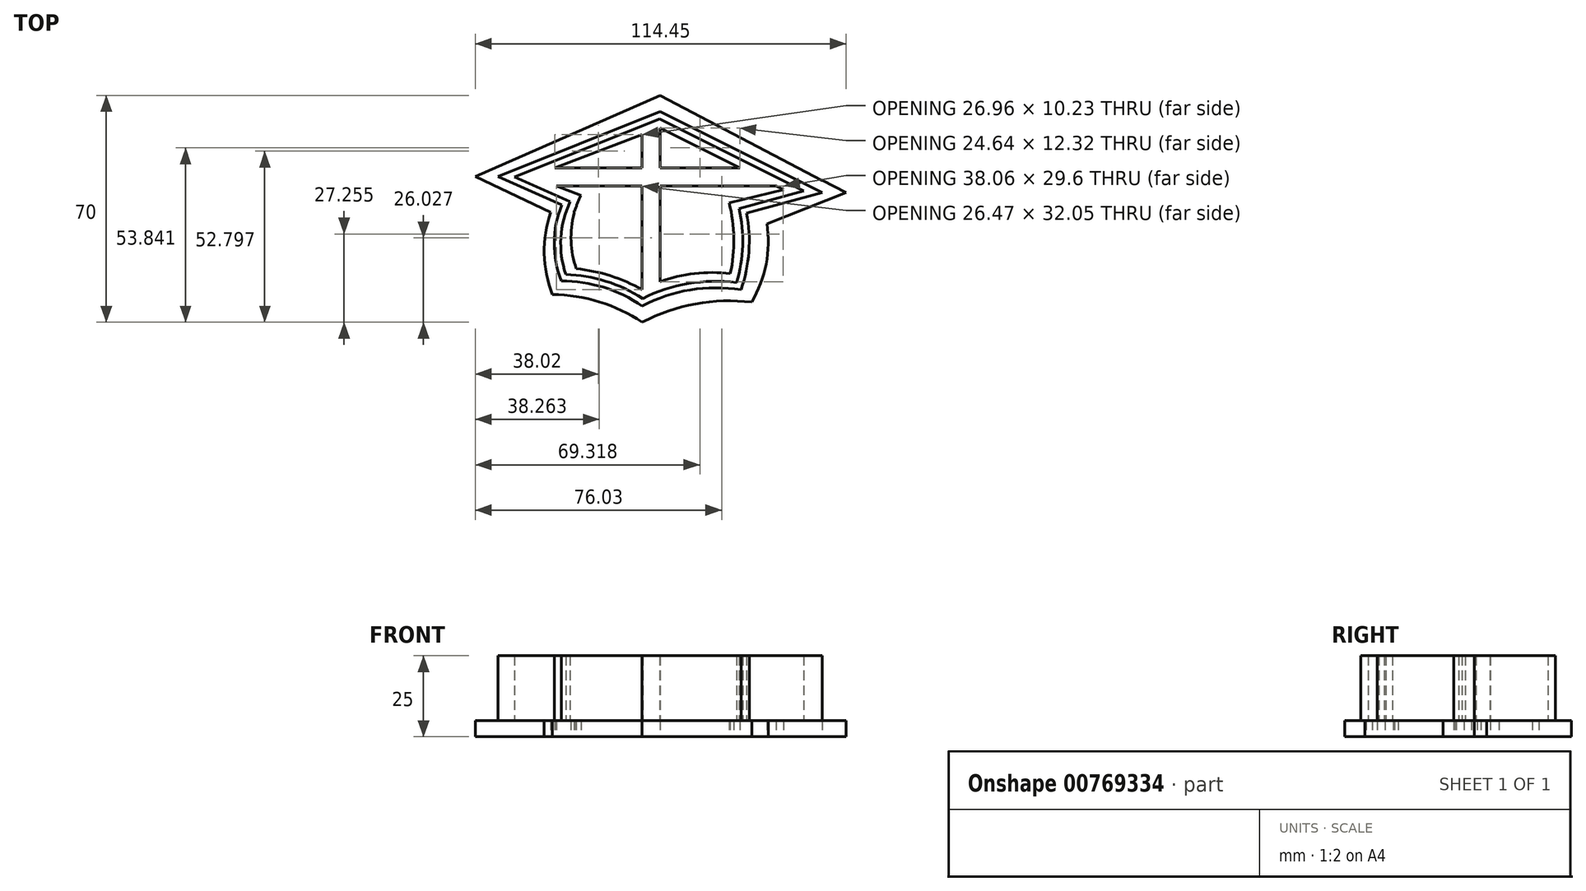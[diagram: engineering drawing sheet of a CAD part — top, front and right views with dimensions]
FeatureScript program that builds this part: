
annotation { "Feature Type Name" : "Feature", "Feature Type Description" : "" }
export const myFeature = defineFeature(function(context is Context, id is Id, definition is map)
    precondition{}
    {
        {
            var Q0;
            Q0=qCreatedBy(makeId("Top.planeOp"),FACE);
            var sketch = newSketch(context, id + "F0", { "sketchPlane" : qUnion([Q0])});
            skLineSegment(sketch, "E0.bottom", {"start": v(50, 50) * mm, "end": v(-50, 50) * mm});
            skLineSegment(sketch, "E0.top", {"start": v(50, -50) * mm, "end": v(-50, -50) * mm});
            skLineSegment(sketch, "E0.left", {"start": v(50, 50) * mm, "end": v(50, -50) * mm});
            skLineSegment(sketch, "E0.right", {"start": v(-50, 50) * mm, "end": v(-50, -50) * mm});
            skPoint(sketch, "E0.middle", {"position": v(0, 0) * mm});
            skLineSegment(sketch, "E1", {"start": v(0, 32.68) * mm, "end": v(0, 30) * mm});
            skLineSegment(sketch, "E2", {"start": v(0, 45) * mm, "end": v(0, 25) * mm});
            skLineSegment(sketch, "E3", {"start": v(35, 25) * mm, "end": v(34.13, 25) * mm});
            skLineSegment(sketch, "E4", {"start": v(0, -10) * mm, "end": v(-5.5, -10) * mm});
            skLineSegment(sketch, "E5", {"start": v(-5.5, -10) * mm, "end": v(-5.5, -5) * mm});
            skArc(sketch, "E6", {"start": v(25, -5) * mm, "mid": v(9.34, -5.03) * mm, "end": v(-5.5, -10) * mm});
            skArc(sketch, "E7", {"start": v(25, -5) * mm, "mid": v(27.54, 10) * mm, "end": v(25, 25) * mm});
            skLineSegment(sketch, "E8", {"start": v(0, 45) * mm, "end": v(0, 10) * mm});
            skLineSegment(sketch, "E9", {"start": v(-50, 30) * mm, "end": v(0, 50) * mm});
            skLineSegment(sketch, "E10", {"start": v(50, 25) * mm, "end": v(0, 50) * mm});
            skLineSegment(sketch, "E11", {"start": v(0, 45) * mm, "end": v(0, 32.68) * mm});
            skLineSegment(sketch, "E12", {"start": v(-50, 30) * mm, "end": v(-30.35, 21.17) * mm});
            skLineSegment(sketch, "E13", {"start": v(50, 25) * mm, "end": v(22.23, 17.5) * mm});
            skLineSegment(sketch, "E14", {"start": v(-5.5, -10) * mm, "end": v(-5.5, -2.25) * mm});
            skPoint(sketch, "E14.endSnap0", {"position": v(-5.5, -7.5) * mm});
            skLineSegment(sketch, "E15", {"start": v(-5.5, -2.25) * mm, "end": v(-30.5, -2.25) * mm});
            skLineSegment(sketch, "E16", {"start": v(-30.5, -2.25) * mm, "end": v(-26.5, -2.25) * mm});
            skLineSegment(sketch, "E17", {"start": v(-26.5, -2.25) * mm, "end": v(-26.5, 3.69) * mm});
            skArc(sketch, "E18", {"start": v(-5.5, -10) * mm, "mid": v(-17.41, -4.23) * mm, "end": v(-30.5, -2.25) * mm});
            skArc(sketch, "E19", {"start": v(-30.35, 21.17) * mm, "mid": v(-32.65, 9.47) * mm, "end": v(-30.5, -2.25) * mm});
            skLineSegment(sketch, "E20", {"start": v(35, 20.95) * mm, "end": v(35.5, 20.95) * mm});
            skLineSegment(sketch, "E21", {"start": v(0, 55) * mm, "end": v(57, 25) * mm});
            skLineSegment(sketch, "E22", {"start": v(-57, 30) * mm, "end": v(0, 55) * mm});
            skLineSegment(sketch, "E23", {"start": v(-57, 30) * mm, "end": v(-33.7, 18.9) * mm});
            skArc(sketch, "E24", {"start": v(-33.7, 18.9) * mm, "mid": v(-35.75, 6.17) * mm, "end": v(-33.19, -6.47) * mm});
            skLineSegment(sketch, "E25", {"start": v(-5.5, -10) * mm, "end": v(-5.5, -15) * mm});
            skArc(sketch, "E26", {"start": v(-5.5, -15) * mm, "mid": v(-18.72, -8.73) * mm, "end": v(-33.19, -6.47) * mm});
            skLineSegment(sketch, "E27", {"start": v(33.01, 15.41) * mm, "end": v(57.45, 25) * mm});
            skArc(sketch, "E28", {"start": v(28.28, -8.77) * mm, "mid": v(32.74, 2.91) * mm, "end": v(33.01, 15.41) * mm});
            skArc(sketch, "E29", {"start": v(28.28, -8.77) * mm, "mid": v(10.93, -9.38) * mm, "end": v(-5.5, -15) * mm});
            skLineSegment(sketch, "E30", {"start": v(0, 45) * mm, "end": v(-39.53, 30) * mm});
            skLineSegment(sketch, "E31", {"start": v(-39.53, 30) * mm, "end": v(-24.42, 24.1) * mm});
            skLineSegment(sketch, "E32", {"start": v(0, 45) * mm, "end": v(38.06, 25.97) * mm});
            skLineSegment(sketch, "E33", {"start": v(38.06, 25.97) * mm, "end": v(21.32, 21.84) * mm});
            skArc(sketch, "E34", {"start": v(-24.42, 24.1) * mm, "mid": v(-27.43, 12.95) * mm, "end": v(-25.83, 1.51) * mm});
            skArc(sketch, "E35", {"start": v(-5.5, -5) * mm, "mid": v(-15.32, -0.68) * mm, "end": v(-25.83, 1.51) * mm});
            skArc(sketch, "E36", {"start": v(21.68, 0) * mm, "mid": v(7.7, -0.42) * mm, "end": v(-5.5, -5) * mm});
            skArc(sketch, "E37", {"start": v(21.68, 0) * mm, "mid": v(22.8, 10.94) * mm, "end": v(21.32, 21.84) * mm});
            skLineSegment(sketch, "E38", {"start": v(-5.5, -5) * mm, "end": v(-5.5, 27.05) * mm});
            skPoint(sketch, "E39.endSnap0", {"position": v(2, -5) * mm});
            skLineSegment(sketch, "E40", {"start": v(-31.97, 27.05) * mm, "end": v(-5.5, 27.05) * mm});
            skLineSegment(sketch, "E41", {"start": v(35.9, 27.05) * mm, "end": v(24.64, 32.68) * mm});
            skLineSegment(sketch, "E42", {"start": v(24.64, 32.68) * mm, "end": v(0, 32.68) * mm});
            skLineSegment(sketch, "E43.trimOffspring", {"start": v(34.13, 25) * mm, "end": v(35, 25) * mm});
            skPoint(sketch, "E44.orphan", {"position": v(-37.04, 16.62) * mm});
            skPoint(sketch, "E45.orphan", {"position": v(2, 44) * mm});
            skPoint(sketch, "E46.trimOffspring.end.orphan", {"position": v(9.5, -5) * mm});
            skPoint(sketch, "E47.orphan", {"position": v(-30.35, 15) * mm});
            skLineSegment(sketch, "E48.trimOffspring", {"start": v(-26.5, 18.63) * mm, "end": v(-26.5, 19.44) * mm});
            skLineSegment(sketch, "E49.trimOffspring", {"start": v(-26.5, 19.44) * mm, "end": v(-26.3, 19.35) * mm});
            skLineSegment(sketch, "E50.trimOffspring", {"start": v(-5.5, 32.68) * mm, "end": v(-5.5, 42.91) * mm});
            skLineSegment(sketch, "E51.trimOffspring", {"start": v(-5.5, 32.68) * mm, "end": v(-32.46, 32.68) * mm});
            skLineSegment(sketch, "E52.trimOffspring", {"start": v(0, 27.05) * mm, "end": v(35.9, 27.05) * mm});
            skLineSegment(sketch, "E53.trimOffspring", {"start": v(0, 30) * mm, "end": v(0, 15) * mm});
            skLineSegment(sketch, "E54.trimOffspring", {"start": v(0, 30) * mm, "end": v(0, 10) * mm});
            skLineSegment(sketch, "E55", {"start": v(0, 10) * mm, "end": v(0, -2.54) * mm});
            skLineSegment(sketch, "E56", {"start": v(26.7, 18.7) * mm, "end": v(50, 25) * mm});
            skLineSegment(sketch, "E57", {"start": v(0, 55) * mm, "end": v(57.45, 25) * mm});
            skSolve(sketch);
        }
        {
            var Q0;
            Q0=makeQuery(id+"F0.imprint","IMPRINT",FACE,{"disambiguationData":[TD([[makeQuery(id+"F0.imprint","IMPRINT",EDGE,{"derivedFrom":sQuery(id+"F0.wireOp",EDGE,"E9")}),-1.0]])]});
            var Q1;
            {var subQ3=sQuery(id+"F0.wireOp",EDGE,"E17");Q1=makeQuery(id+"F0.imprint","IMPRINT",FACE,{"disambiguationData":[TD([[makeQuery(id+"F0.imprint","IMPRINT",EDGE,{"derivedFrom":subQ3}),-1.0]])]});}
            var Q2;
            {var subQ6=sQuery(id+"F0.wireOp",EDGE,"E5");Q2=makeQuery(id+"F0.imprint","IMPRINT",FACE,{"disambiguationData":[TD([[makeQuery(id+"F0.imprint","IMPRINT",EDGE,{"derivedFrom":subQ6}),-1.0]])]});}
            var Q3;
            {var subQ5=sQuery(id+"F0.wireOp",EDGE,"E5");Q3=makeQuery(id+"F0.imprint","IMPRINT",FACE,{"disambiguationData":[TD([[makeQuery(id+"F0.imprint","IMPRINT",EDGE,{"derivedFrom":subQ5}),1.0]])]});}
            var Q4;
            {var subQ0=sQuery(id+"F0.wireOp",EDGE,"E14");Q4=makeQuery(id+"F0.imprint","IMPRINT",FACE,{"disambiguationData":[TD([[makeQuery(id+"F0.imprint","IMPRINT",EDGE,{"derivedFrom":subQ0}),1.0]])]});}
            var Q5;
            {var subQ14=sQuery(id+"F0.wireOp",EDGE,"E1");Q5=makeQuery(id+"F0.imprint","IMPRINT",FACE,{"disambiguationData":[TD([[makeQuery(id+"F0.imprint","IMPRINT",EDGE,{"derivedFrom":subQ14}),-1.0]])]});}
            var Q6;
            {var subQ15=sQuery(id+"F0.wireOp",EDGE,"E52.trimOffspring");Q6=makeQuery(id+"F0.imprint","IMPRINT",FACE,{"disambiguationData":[TD([[makeQuery(id+"F0.imprint","IMPRINT",EDGE,{"derivedFrom":subQ15}),-1.0]])]});}
            var Q7;
            {var subQ0=sQuery(id+"F0.wireOp",EDGE,"E13");var subQ1=sQuery(id+"F0.wireOp",EDGE,"E7");var subQ2=makeQuery(id+"F0.imprint","INTERSECT",VERTEX,{"derivedFrom":[subQ1,subQ0]});Q7=makeQuery(id+"F0.imprint","IMPRINT",FACE,{"disambiguationData":[TD([[makeQuery(id+"F0.imprint","IMPRINT",EDGE,{"disambiguationData":[TD([[subQ2,-1.0]])],"derivedFrom":subQ1}),1.0]])]});}
            var Q8;
            {var subQ4=sQuery(id+"F0.wireOp",EDGE,"E1");Q8=makeQuery(id+"F0.imprint","IMPRINT",FACE,{"disambiguationData":[TD([[makeQuery(id+"F0.imprint","IMPRINT",EDGE,{"derivedFrom":subQ4}),1.0]])]});}
            var Q9;
            {var subQ0=sQuery(id+"F0.wireOp",EDGE,"E42");Q9=makeQuery(id+"F0.imprint","IMPRINT",FACE,{"disambiguationData":[TD([[makeQuery(id+"F0.imprint","IMPRINT",EDGE,{"derivedFrom":subQ0}),-1.0]])]});}
            var Q10;
            {var subQ0=sQuery(id+"F0.wireOp",EDGE,"E50.trimOffspring");Q10=makeQuery(id+"F0.imprint","IMPRINT",FACE,{"disambiguationData":[TD([[makeQuery(id+"F0.imprint","IMPRINT",EDGE,{"derivedFrom":subQ0}),1.0]])]});}
            var Q11;
            {var subQ6=sQuery(id+"F0.wireOp",EDGE,"E38");Q11=makeQuery(id+"F0.imprint","IMPRINT",FACE,{"disambiguationData":[TD([[makeQuery(id+"F0.imprint","IMPRINT",EDGE,{"derivedFrom":subQ6}),1.0]])]});}
            var Q12;
            {var subQ0=sQuery(id+"F0.wireOp",EDGE,"E48.trimOffspring");Q12=makeQuery(id+"F0.imprint","IMPRINT",FACE,{"disambiguationData":[TD([[makeQuery(id+"F0.imprint","IMPRINT",EDGE,{"derivedFrom":subQ0}),-1.0]])]});}
            extrude(context, id + "F1", {"entities" : qUnion([Q0, Q1, Q2, Q3, Q4, Q5, Q6, Q7, Q8, Q9, Q10, Q11, Q12]), "depth" : 25 * mm, "offsetDistance" : 25 * mm});
        }
        {
            var Q0;
            Q0=makeQuery(id+"F1.opExtrude","CAP_FACE",FACE,{"disambiguationData":[OSD([sQuery(id+"F0.wireOp",EDGE,"E6"),sQuery(id+"F0.wireOp",EDGE,"E7"),sQuery(id+"F0.wireOp",EDGE,"E9"),sQuery(id+"F0.wireOp",EDGE,"E10"),sQuery(id+"F0.wireOp",EDGE,"E12"),sQuery(id+"F0.wireOp",EDGE,"E13"),sQuery(id+"F0.wireOp",EDGE,"E18"),sQuery(id+"F0.wireOp",EDGE,"E19")])],"isStart":false});
            shell(context, id + "F2", {"entities" : qUnion([Q0]), "thickness" : 2 * mm});
        }
        {
            var Q0;
            {var subQ6=sQuery(id+"F0.wireOp",EDGE,"E6");Q0=makeQuery(id+"F0.imprint","IMPRINT",FACE,{"disambiguationData":[TD([[makeQuery(id+"F0.imprint","IMPRINT",EDGE,{"derivedFrom":subQ6}),1.0]])]});}
            var Q1;
            {var subQ3=sQuery(id+"F0.wireOp",EDGE,"E10");Q1=makeQuery(id+"F0.imprint","IMPRINT",FACE,{"disambiguationData":[TD([[makeQuery(id+"F0.imprint","IMPRINT",EDGE,{"derivedFrom":subQ3}),-1.0]])]});}
            var Q2;
            {var subQ0=sQuery(id+"F0.wireOp",EDGE,"E0.bottom");var subQ2=sQuery(id+"F0.wireOp",EDGE,"E22");var subQ3=makeQuery(id+"F0.imprint","INTERSECT",VERTEX,{"derivedFrom":[subQ0,subQ2]});Q2=makeQuery(id+"F0.imprint","IMPRINT",FACE,{"disambiguationData":[TD([[makeQuery(id+"F0.imprint","IMPRINT",EDGE,{"disambiguationData":[TD([[subQ3,1.0]])],"derivedFrom":subQ0}),-1.0]])]});}
            var Q3;
            {var subQ0=sQuery(id+"F0.wireOp",EDGE,"E9");Q3=makeQuery(id+"F0.imprint","IMPRINT",FACE,{"disambiguationData":[TD([[makeQuery(id+"F0.imprint","IMPRINT",EDGE,{"derivedFrom":subQ0}),1.0]])]});}
            var Q4;
            {var subQ1=sQuery(id+"F0.wireOp",EDGE,"E0.right");var subQ4=sQuery(id+"F0.wireOp",EDGE,"E22");var subQ5=makeQuery(id+"F0.imprint","INTERSECT",VERTEX,{"derivedFrom":[subQ1,subQ4]});Q4=makeQuery(id+"F0.imprint","IMPRINT",FACE,{"disambiguationData":[TD([[makeQuery(id+"F0.imprint","IMPRINT",EDGE,{"disambiguationData":[TD([[subQ5,1.0]])],"derivedFrom":subQ4}),-1.0]])]});}
            var Q5;
            {var subQ0=sQuery(id+"F0.wireOp",EDGE,"E12");Q5=makeQuery(id+"F0.imprint","IMPRINT",FACE,{"disambiguationData":[TD([[makeQuery(id+"F0.imprint","IMPRINT",EDGE,{"derivedFrom":subQ0}),-1.0]])]});}
            var Q6;
            {var subQ6=sQuery(id+"F0.wireOp",EDGE,"E5");Q6=makeQuery(id+"F0.imprint","IMPRINT",FACE,{"disambiguationData":[TD([[makeQuery(id+"F0.imprint","IMPRINT",EDGE,{"derivedFrom":subQ6}),-1.0]])]});}
            var Q7;
            {var subQ5=sQuery(id+"F0.wireOp",EDGE,"E5");Q7=makeQuery(id+"F0.imprint","IMPRINT",FACE,{"disambiguationData":[TD([[makeQuery(id+"F0.imprint","IMPRINT",EDGE,{"derivedFrom":subQ5}),1.0]])]});}
            var Q8;
            {var subQ3=sQuery(id+"F0.wireOp",EDGE,"E17");Q8=makeQuery(id+"F0.imprint","IMPRINT",FACE,{"disambiguationData":[TD([[makeQuery(id+"F0.imprint","IMPRINT",EDGE,{"derivedFrom":subQ3}),-1.0]])]});}
            var Q9;
            Q9=makeQuery(id+"F0.imprint","IMPRINT",FACE,{"disambiguationData":[TD([[makeQuery(id+"F0.imprint","IMPRINT",EDGE,{"derivedFrom":sQuery(id+"F0.wireOp",EDGE,"E9")}),-1.0]])]});
            var Q10;
            {var subQ0=sQuery(id+"F0.wireOp",EDGE,"E13");var subQ1=sQuery(id+"F0.wireOp",EDGE,"E7");var subQ2=makeQuery(id+"F0.imprint","INTERSECT",VERTEX,{"derivedFrom":[subQ1,subQ0]});Q10=makeQuery(id+"F0.imprint","IMPRINT",FACE,{"disambiguationData":[TD([[makeQuery(id+"F0.imprint","IMPRINT",EDGE,{"disambiguationData":[TD([[subQ2,-1.0]])],"derivedFrom":subQ1}),1.0]])]});}
            var Q11;
            {var subQ14=sQuery(id+"F0.wireOp",EDGE,"E1");Q11=makeQuery(id+"F0.imprint","IMPRINT",FACE,{"disambiguationData":[TD([[makeQuery(id+"F0.imprint","IMPRINT",EDGE,{"derivedFrom":subQ14}),-1.0]])]});}
            var Q12;
            {var subQ4=sQuery(id+"F0.wireOp",EDGE,"E1");Q12=makeQuery(id+"F0.imprint","IMPRINT",FACE,{"disambiguationData":[TD([[makeQuery(id+"F0.imprint","IMPRINT",EDGE,{"derivedFrom":subQ4}),1.0]])]});}
            var Q13;
            {var subQ0=sQuery(id+"F0.wireOp",EDGE,"E0.left");var subQ1=makeQuery(id+"F0.imprint","INTERSECT",VERTEX,{"derivedFrom":[subQ0,sQuery(id+"F0.wireOp",EDGE,"E21")]});Q13=makeQuery(id+"F0.imprint","IMPRINT",FACE,{"disambiguationData":[TD([[makeQuery(id+"F0.imprint","IMPRINT",EDGE,{"disambiguationData":[TD([[subQ1,1.0]])],"derivedFrom":subQ0}),1.0]])]});}
            extrude(context, id + "F3", {"entities" : qUnion([Q0, Q1, Q2, Q3, Q4, Q5, Q6, Q7, Q8, Q9, Q10, Q11, Q12, Q13]), "operationType" : NewBodyOperationType.ADD, "depth" : 5 * mm, "offsetDistance" : 25 * mm});
        }
        {
            var Q0;
            {var subQ1=sQuery(id+"F0.wireOp",EDGE,"E31");Q0=makeQuery(id+"F3.boolean.opBoolean","SPLIT",FACE,{"disambiguationData":[TD([makeQuery(id+"F3.opExtrude","SWEPT_FACE",FACE,{"disambiguationData":[OSD([subQ1])]})])],"derivedFrom":makeQuery(id+"F2.opShell","OFFSET_FACE",FACE,{"disambiguationData":[OSD([sQuery(id+"F0.wireOp",EDGE,"E6"),sQuery(id+"F0.wireOp",EDGE,"E7"),sQuery(id+"F0.wireOp",EDGE,"E9"),sQuery(id+"F0.wireOp",EDGE,"E10"),sQuery(id+"F0.wireOp",EDGE,"E12"),sQuery(id+"F0.wireOp",EDGE,"E13"),sQuery(id+"F0.wireOp",EDGE,"E18"),sQuery(id+"F0.wireOp",EDGE,"E19")])]})});}
            var Q1;
            {var subQ0=sQuery(id+"F0.wireOp",EDGE,"E33");Q1=makeQuery(id+"F3.boolean.opBoolean","SPLIT",FACE,{"disambiguationData":[TD([makeQuery(id+"F3.opExtrude","SWEPT_FACE",FACE,{"disambiguationData":[OSD([subQ0])]})])],"derivedFrom":makeQuery(id+"F2.opShell","OFFSET_FACE",FACE,{"disambiguationData":[OSD([sQuery(id+"F0.wireOp",EDGE,"E6"),sQuery(id+"F0.wireOp",EDGE,"E7"),sQuery(id+"F0.wireOp",EDGE,"E9"),sQuery(id+"F0.wireOp",EDGE,"E10"),sQuery(id+"F0.wireOp",EDGE,"E12"),sQuery(id+"F0.wireOp",EDGE,"E13"),sQuery(id+"F0.wireOp",EDGE,"E18"),sQuery(id+"F0.wireOp",EDGE,"E19")])]})});}
            var Q2;
            {var subQ0=sQuery(id+"F0.wireOp",EDGE,"E2");Q2=makeQuery(id+"F3.boolean.opBoolean","SPLIT",FACE,{"disambiguationData":[TD([makeQuery(id+"F3.opExtrude","SWEPT_FACE",FACE,{"disambiguationData":[OSD([subQ0])]})])],"derivedFrom":makeQuery(id+"F2.opShell","OFFSET_FACE",FACE,{"disambiguationData":[OSD([sQuery(id+"F0.wireOp",EDGE,"E6"),sQuery(id+"F0.wireOp",EDGE,"E7"),sQuery(id+"F0.wireOp",EDGE,"E9"),sQuery(id+"F0.wireOp",EDGE,"E10"),sQuery(id+"F0.wireOp",EDGE,"E12"),sQuery(id+"F0.wireOp",EDGE,"E13"),sQuery(id+"F0.wireOp",EDGE,"E18"),sQuery(id+"F0.wireOp",EDGE,"E19")])]})});}
            var Q3;
            Q3=makeQuery(id+"F3.boolean.opBoolean","SPLIT",FACE,{"disambiguationData":[TD([makeQuery(id+"F3.opExtrude","SWEPT_FACE",FACE,{"disambiguationData":[OSD([sQuery(id+"F0.wireOp",EDGE,"E30")])]})])],"derivedFrom":makeQuery(id+"F2.opShell","OFFSET_FACE",FACE,{"disambiguationData":[OSD([sQuery(id+"F0.wireOp",EDGE,"E6"),sQuery(id+"F0.wireOp",EDGE,"E7"),sQuery(id+"F0.wireOp",EDGE,"E9"),sQuery(id+"F0.wireOp",EDGE,"E10"),sQuery(id+"F0.wireOp",EDGE,"E12"),sQuery(id+"F0.wireOp",EDGE,"E13"),sQuery(id+"F0.wireOp",EDGE,"E18"),sQuery(id+"F0.wireOp",EDGE,"E19")])]})});
            extrude(context, id + "F4", {"entities" : qUnion([Q0, Q1, Q2, Q3]), "operationType" : NewBodyOperationType.REMOVE, "endBound" : BoundingType.THROUGH_ALL, "oppositeDirection" : true, "depth" : 25 * mm, "offsetDistance" : 25 * mm});
        }
    });
